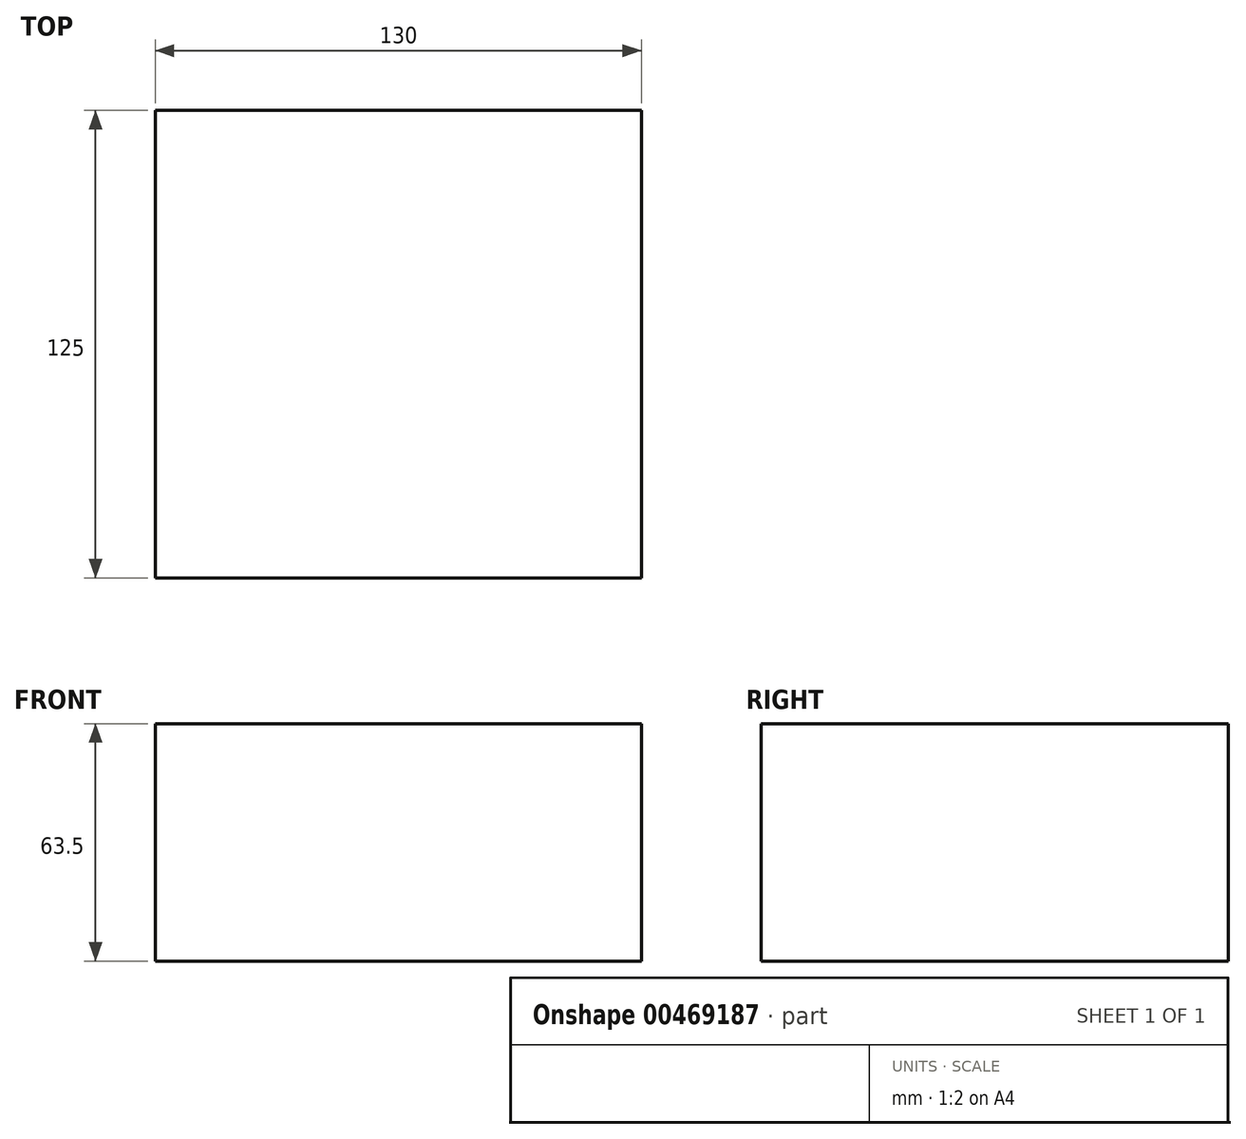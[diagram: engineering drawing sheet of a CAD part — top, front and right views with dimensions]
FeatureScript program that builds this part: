
annotation { "Feature Type Name" : "Feature", "Feature Type Description" : "" }
export const myFeature = defineFeature(function(context is Context, id is Id, definition is map)
    precondition{}
    {
        {
            var Q0;
            Q0=qCreatedBy(makeId("Top.planeOp"),FACE);
            var sketch = newSketch(context, id + "F0", { "sketchPlane" : qUnion([Q0])});
            skLineSegment(sketch, "E0.bottom", {"start": v(0, 0) * mm, "end": v(130, 0) * mm});
            skLineSegment(sketch, "E0.top", {"start": v(0, 125) * mm, "end": v(130, 125) * mm});
            skLineSegment(sketch, "E0.left", {"start": v(0, 0) * mm, "end": v(0, 125) * mm});
            skLineSegment(sketch, "E0.right", {"start": v(130, 0) * mm, "end": v(130, 125) * mm});
            skSolve(sketch);
        }
        {
            var Q0;
            Q0 = qSketchRegion(id + "F0", true);
            extrude(context, id + "F1", {"entities" : qUnion([Q0]), "depth" : 63.5 * mm});
        }
    });
